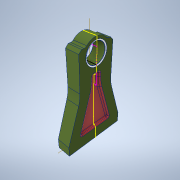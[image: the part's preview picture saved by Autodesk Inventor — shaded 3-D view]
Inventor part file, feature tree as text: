
AUTODESK INVENTOR PART (.ipt)
format: ipt  version: 2021.1 (Build 251245000, 245)  size: 306,176 bytes
history: native  units: in
note: dims shown in document units (in); Inventor stores cm internally (conversion verified against a paired STEP export)
features: sketch x5, extrude x4, projected_geometry x4, fillet x2, thread x2, chamfer x2, mirror x1
ambient origin geometry x8: Origin, YZ Plane, XZ Plane, XY Plane, X Axis, Y Axis, Z Axis, Center Point
bodies: Solid1 (feature_tree)
feature tree (20):
  extrude  "Extrusion1"  Depth=9.2in
  sketch  "Sketch2"  dims[d2=1.5in d3=6.5in]
  extrude  "Extrusion2"  Depth=6.5in
  extrude  "Extrusion3"  Depth=13.7in
  fillet  "Fillet1"  Radius=0.125in
  mirror  "Mirror1"
  fillet  "Fillet2"  Radius=5.0in
  extrude  "Extrusion4"  Depth=0.5in
  thread  "Thread1"  [1 undecoded]
  thread  "Thread2"  [1 undecoded]
  sketch  "Sketch4"  dims[d8=4.0in d9=12.5in d10=0.5in d11=0.5in]
  sketch  "Sketch7"  dims[d12=0.4in d13=45.0deg d14=0.4in d15=45.0deg d16=2.0in d17=0.0in d18=2.8in d20=0.0082in d21=0.0082in d22=2.0in d23=6.5in d25=6.5in d26=10.0in d27=2.0in d28=2.0in d29=5.0in d30=0.2in d31=2.0in d32=0.0in d33=0.4in d34=0.0in d35=0.2in d36=0.2in d37=1.0in d38=1.0in d39=6.0in d40=2.0in d41=0.0in d42=2.0in d43=0.0in d44=2.0in d45=0.0in d49=0.1in d50=0.125in d51=45.0deg d52=0.1in d53=0.125in d54=45.0deg]
  chamfer  "Chamfer1"  Angle=45.0deg  [1 undecoded]
  chamfer  "Chamfer2"  Distance=0.4in
  sketch  "Sketch1"  dims[d0=9.2in d1=1.5in]
  sketch  "Sketch3"  dims[d4=6.5in d5=13.7in d6=0.125in d7=5.0in]
  projected_geometry  "Projected Loop1"
  projected_geometry  "Projected Loop2"
  projected_geometry  "Project Cut Edges1"
  projected_geometry  "Project Cut Edges2"
note: 3 required parameter values undecoded (feature->parameter linkage not recoverable at this tier; creation-order binding heuristic only, values carry confidence <= 0.55)
